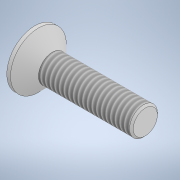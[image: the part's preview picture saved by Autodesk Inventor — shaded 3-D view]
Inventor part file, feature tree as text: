
AUTODESK INVENTOR PART (.ipt)
format: ipt  version: 2022 (Build 260153000, 153)  size: 130,048 bytes
history: native  units: mm
features: sketch x2, revolve x1, extrude x1, thread x1, chamfer x1
ambient origin geometry x8: Origin, YZ Plane, XZ Plane, XY Plane, X Axis, Y Axis, Z Axis, Center Point
bodies: Solid1 (feature_tree)
feature tree (6):
  revolve  "Revolution1"  Angle=45.0deg
  extrude  "Extrusion1"  Depth=1.5mm
  thread  "Thread1"  [1 undecoded]
  chamfer  "Chamfer1"  Angle=90.0deg  [1 undecoded]
  sketch  "Sketch1"  dims[d0=10.0mm d1=45.0deg]
  sketch  "Sketch2"  dims[d2=1.9mm d3=1.5mm d4=3.0mm d5=90.0deg d6=2.0mm d7=1.2mm d8=0.0mm d9=10.0mm d10=0.0mm d11=0.2mm d12=2.0mm d13=45.0deg]
note: 2 required parameter values undecoded (feature->parameter linkage not recoverable at this tier; creation-order binding heuristic only, values carry confidence <= 0.55)
